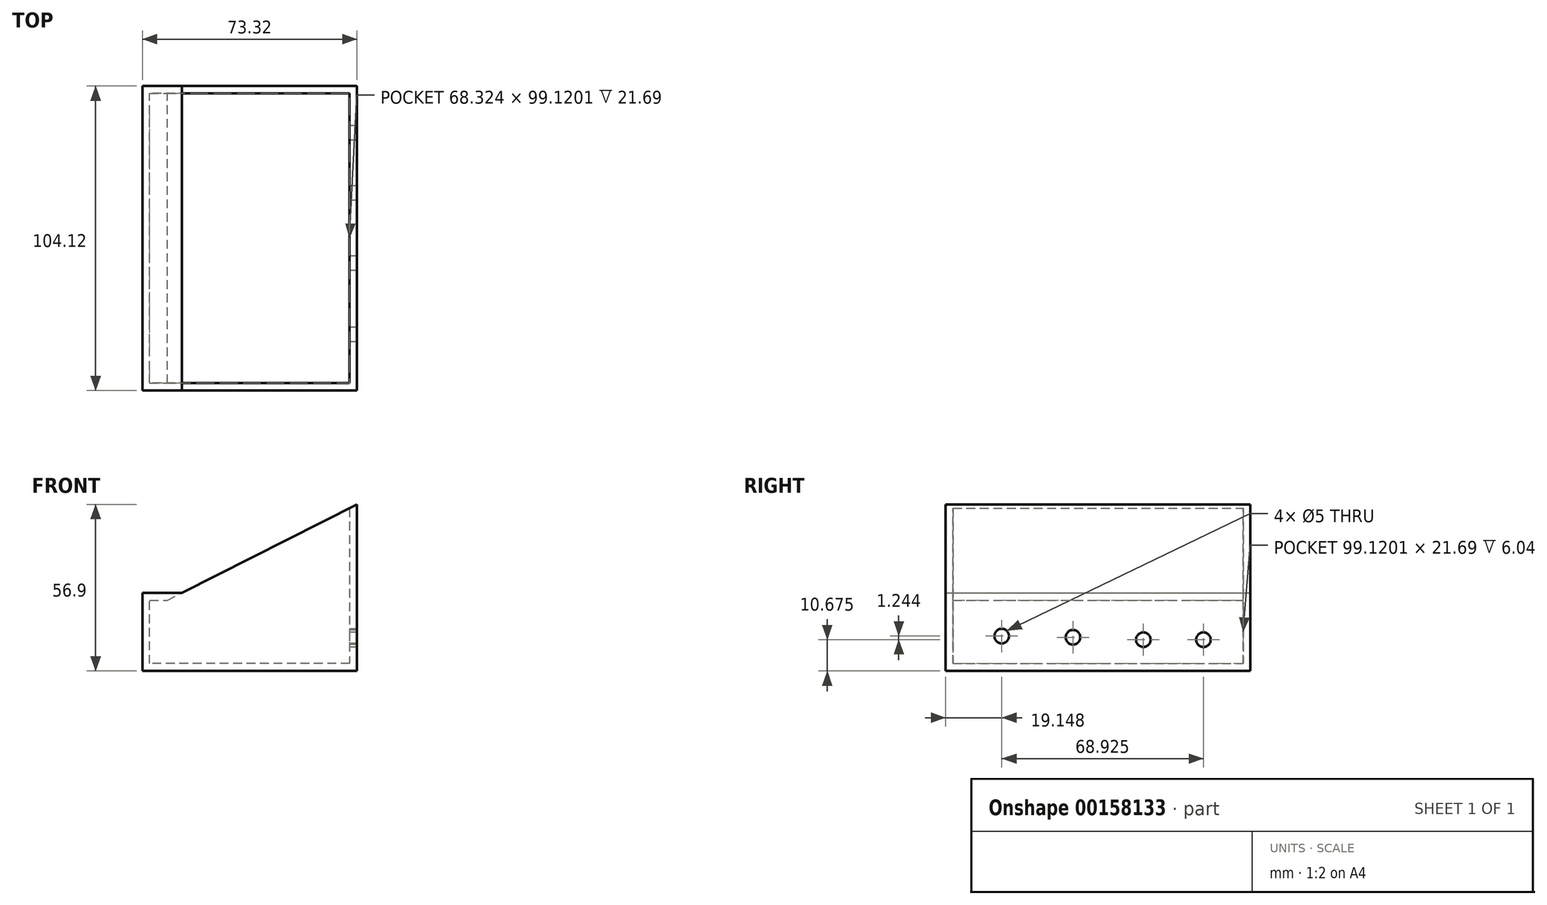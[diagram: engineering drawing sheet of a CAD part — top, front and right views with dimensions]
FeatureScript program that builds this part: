
annotation { "Feature Type Name" : "Feature", "Feature Type Description" : "" }
export const myFeature = defineFeature(function(context is Context, id is Id, definition is map)
    precondition{}
    {
        {
            var Q0;
            Q0=qCreatedBy(makeId("Front.planeOp"),FACE);
            var sketch = newSketch(context, id + "F0", { "sketchPlane" : qUnion([Q0])});
            skLineSegment(sketch, "E0", {"start": v(26.69, 35.93) * mm, "end": v(26.69, -20.97) * mm});
            skLineSegment(sketch, "E1", {"start": v(26.69, -20.97) * mm, "end": v(-46.63, -20.97) * mm});
            skLineSegment(sketch, "E2", {"start": v(-46.63, -20.97) * mm, "end": v(-46.63, 0) * mm});
            skLineSegment(sketch, "E3", {"start": v(-46.63, 0) * mm, "end": v(-46.63, 5.72) * mm});
            skLineSegment(sketch, "E4", {"start": v(-46.63, 5.72) * mm, "end": v(-33.14, 5.72) * mm});
            skLineSegment(sketch, "E5", {"start": v(-33.14, 5.72) * mm, "end": v(26.69, 35.93) * mm});
            skSolve(sketch);
        }
        {
            var Q0;
            Q0=qCreatedBy(makeId("Right.planeOp"),FACE);
            var sketch = newSketch(context, id + "F1", { "sketchPlane" : qUnion([Q0])});
            skLineSegment(sketch, "E6", {"start": v(104.12, 37.69) * mm, "end": v(0, 37.69) * mm});
            skLineSegment(sketch, "E7", {"start": v(0, 37.69) * mm, "end": v(0, -21.56) * mm});
            skLineSegment(sketch, "E8", {"start": v(0, -21.56) * mm, "end": v(104.12, -21.56) * mm});
            skLineSegment(sketch, "E9", {"start": v(104.12, -21.56) * mm, "end": v(104.12, 37.69) * mm});
            skSolve(sketch);
        }
        {
            var Q0;
            Q0=makeQuery(id+"F0.imprint","IMPRINT",FACE,{"disambiguationData":[TD([[makeQuery(id+"F0.imprint","IMPRINT",EDGE,{"derivedFrom":sQuery(id+"F0.wireOp",EDGE,"E0")}),-1.0]])]});
            var Q1;
            Q1=sQuery(id+"F1.wireOp",EDGE,"E6");
            sweep(context, id + "F2", {"profiles" : qUnion([Q0]), "path" : qUnion([Q1])});
        }
        {
            var Q0;
            Q0=makeQuery(id+"F2.opSweep","SWEPT_FACE",FACE,{"disambiguationData":[OSD([sQuery(id+"F0.wireOp",EDGE,"E5"),sQuery(id+"F1.wireOp",EDGE,"E6")])]});
            shell(context, id + "F3", {"entities" : qUnion([Q0]), "thickness" : 2.5 * mm});
        }
        {
            var Q0;
            Q0=makeQuery(id+"F3.opShell","OFFSET_FACE",FACE,{"disambiguationData":[OSD([sQuery(id+"F0.wireOp",EDGE,"E0"),sQuery(id+"F1.wireOp",EDGE,"E6")])]});
            var sketch = newSketch(context, id + "F4", { "sketchPlane" : qUnion([Q0])});
            skPoint(sketch, "E10", {"position": v(-88.07, -10.3) * mm});
            skPoint(sketch, "E11", {"position": v(-67.54, -10.3) * mm});
            skPoint(sketch, "E12", {"position": v(-43.5, -9.47) * mm});
            skPoint(sketch, "E13", {"position": v(-19.15, -9.05) * mm});
            skSolve(sketch);
        }
        {
            var Q0;
            Q0=sQuery(id+"F4.wireOp",VERTEX,"E10");
            var Q1;
            Q1=sQuery(id+"F4.wireOp",VERTEX,"E11");
            var Q2;
            Q2=sQuery(id+"F4.wireOp",VERTEX,"E12");
            var Q3;
            Q3=sQuery(id+"F4.wireOp",VERTEX,"E13");
            var Q4;
            Q4=makeQuery(id+"F2.opSweep","SWEPT_BODY",BODY,{"disambiguationData":[OSD([sQuery(id+"F0.wireOp",EDGE,"E0"),sQuery(id+"F0.wireOp",EDGE,"E1"),sQuery(id+"F0.wireOp",EDGE,"E2"),sQuery(id+"F0.wireOp",EDGE,"E3"),sQuery(id+"F0.wireOp",EDGE,"E4"),sQuery(id+"F0.wireOp",EDGE,"E5"),sQuery(id+"F1.wireOp",EDGE,"E6")])]});
            hole(context, id + "F5", {"style" : HoleStyle.SIMPLE, "endStyle" : HoleEndStyle.BLIND, "holeDiameter" : 5 * mm, "holeDepth" : 12 * mm, "locations" : qUnion([Q0, Q1, Q2, Q3]), "scope" : qUnion([Q4])});
        }
    });
